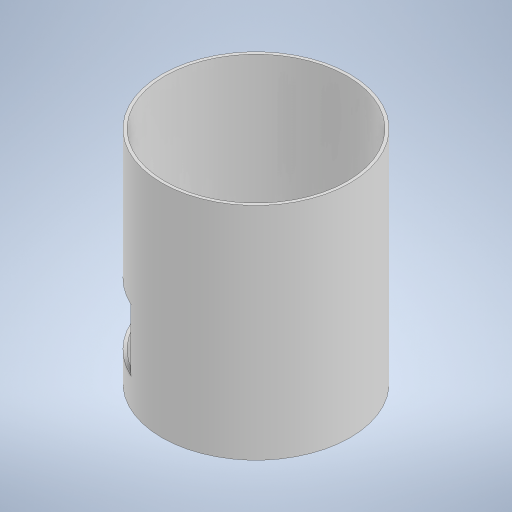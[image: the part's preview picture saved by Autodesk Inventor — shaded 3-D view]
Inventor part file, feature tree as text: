
AUTODESK INVENTOR PART (.ipt)
format: ipt  version: 2024.3 (Build 283343000, 343)  size: 216,576 bytes
history: native  units: mm
features: extrude x2, sketch x2
ambient origin geometry x8: Origin, YZ Plane, XZ Plane, XY Plane, X Axis, Y Axis, Z Axis, Center Point
bodies: Solid1 (feature_tree)
feature tree (4):
  extrude  "Extrusion1"  Depth=128.0mm
  extrude  "Extrusion2"  Depth=42.0mm
  sketch  "Sketch1"  dims[d0=2.0mm d1=128.0mm]
  sketch  "Sketch2"  dims[d2=150.0mm d3=0.0mm d4=42.0mm d5=116.0mm d6=20.0mm d7=58.0mm d8=0.0mm d9=0.0mm]
